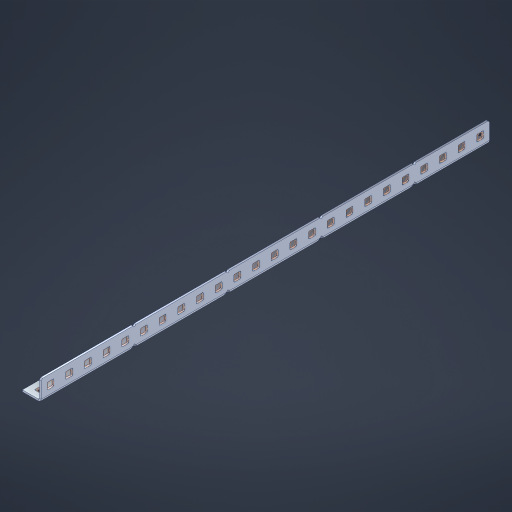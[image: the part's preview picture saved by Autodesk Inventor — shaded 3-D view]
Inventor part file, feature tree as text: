
AUTODESK INVENTOR PART (.ipt)
format: ipt  version: 2023 (Build 270158000, 158)  size: 823,808 bytes
history: native  units: in
note: dims shown in document units (in); Inventor stores cm internally (conversion verified against a paired STEP export)
features: other x53, extrude x47, sheet_metal_op x10, sketch x8, mirror x1, pattern_linear x1, chamfer x1
ambient origin geometry x8: Origin, YZ Plane, XZ Plane, XY Plane, X Axis, Y Axis, Z Axis, Center Point
bodies: Solid1 (feature_tree), Body (feature_tree)
feature tree (121):
  other  "Flange Pattern Plane"
  sheet_metal_op  "Flange Pattern"
  sheet_metal_op  "Body Pattern"
  other  "Arc Length"
  mirror  "Notch Mirror"
  pattern_linear  "Notch Pattern"  Spacing1=0.1875in  [1 undecoded]
  chamfer  "End Chamfer"
  extrude  "Half Cut"  Depth=0.0469in
  sketch  "Sketch1"  dims[d0=2.5in]
  other  "Plate1"
  sketch  "Sketch2"  dims[d1=12.0in]
  other  "Plate2"
  sheet_metal_op  "Bend1"
  sheet_metal_op  "Corner1"
  sketch  "Sketch3"  dims[d2=0.0469in]
  other  "Flange Pattern Sketch"
  sketch  "Sketch7"  dims[d3=0.0469in]
  other  "Srf1"
  other  "Srf2"
  sketch  "Sketch8"  dims[d4=0.0234in]
  sketch  "Sketch9"  dims[d5=0.0938in]
  other  "Srf91"
  sheet_metal_op  "Body Pattern Sketch"
  other  "Srf92"
  sketch  "Sketch13"  dims[d6=0.0469in]
  sketch  "Sketch14"  dims[d7=0.5in d8=90.0deg d9=0.0312in d10=0.1875in d11=0.0469in d12=0.0469in d16=0.182in d17=0.02in d18=0.0469in d19=0.0in d20=0.25in d21=0.25in d46=0.172in d47=1.0in d48=0.0in d49=0.182in d50=0.02in d51=0.25in d52=0.25in d53=0.0469in d54=0.0in d55=0.172in d56=1.0in d57=0.0in d60=9.4488in d62=0.5in d63=0.3937in d65=0.5in d85=0.1227in d86=0.1659in d88=0.04in d89=0.0469in d90=0.0in d91=0.04in d92=0.0491in d95=2.5in d96=0.04in d97=0.25in d98=45.0deg d101=0.0in d102=2.497in d131=0.5in d132=9.4488in d134=0.5in d139=0.5in]
  other  "Srf856"
  other  "Srf1310"
  other  "Srf1311"
  other  "Srf1312"
  other  "Srf1376"
  other  "Srf1377"
  other  "Srf1728"
  other  "Srf1755"
  other  "Srf1878"
  other  "Srf1879"
  other  "Srf1880"
  other  "Srf1881"
  other  "Srf1882"
  other  "Srf1883"
  other  "Srf1884"
  other  "Srf1885"
  other  "Srf1886"
  other  "Srf1887"
  other  "Srf1888"
  other  "Srf1889"
  other  "Srf1890"
  other  "Srf1891"
  other  "Srf1892"
  other  "Srf1893"
  other  "Srf1894"
  other  "Srf1895"
  other  "Srf1942"
  other  "Srf1943"
  other  "Srf1944"
  other  "Srf1945"
  other  "Srf1946"
  other  "Srf1947"
  other  "Srf1948"
  other  "Srf1949"
  other  "Srf1950"
  other  "Srf1951"
  other  "Srf1952"
  other  "Srf1953"
  other  "Srf1954"
  other  "Srf1955"
  other  "Srf1956"
  other  "Srf1957"
  other  "Srf1958"
  other  "Srf1959"
  sheet_metal_op  "Flange Stamp"
  sheet_metal_op  "Flange Circle"
  sheet_metal_op  "Body Stamp"
  sheet_metal_op  "Body Circle"
  sheet_metal_op  "Notch"
  extrude  "ExtrusionSrf2"  Depth=0.0469in
  extrude  "ExtrusionSrf92"  Depth=0.5in
  extrude  "ExtrusionSrf856"  Depth=0.02in
  extrude  "ExtrusionSrf1310"  Depth=0.0469in
  extrude  "ExtrusionSrf1311"  TaperAngle=0.0deg  [1 undecoded]
  extrude  "ExtrusionSrf1312"  Depth=0.5in
  extrude  "ExtrusionSrf1376"  Depth=0.5in
  extrude  "ExtrusionSrf1377"  Depth=0.5in
  extrude  "ExtrusionSrf1728"  Depth=0.5in TaperAngle=0.0deg
  extrude  "ExtrusionSrf1755"  Depth=0.5in
  extrude  "ExtrusionSrf1878"  Depth=0.02in
  extrude  "ExtrusionSrf1879"  Depth=0.5in
  extrude  "ExtrusionSrf1880"  Depth=0.5in
  extrude  "ExtrusionSrf1881"  Depth=0.0469in
  extrude  "ExtrusionSrf1882"  TaperAngle=0.0deg  [1 undecoded]
  extrude  "ExtrusionSrf1883"  Depth=0.5in
  extrude  "ExtrusionSrf1884"  Depth=0.5in TaperAngle=0.0deg
  extrude  "ExtrusionSrf1885"  Depth=0.5in
  extrude  "ExtrusionSrf1886"  Depth=0.5in
  extrude  "ExtrusionSrf1887"  Depth=0.5in
  extrude  "ExtrusionSrf1888"  Depth=0.5in
  extrude  "ExtrusionSrf1889"  Depth=0.5in
  extrude  "ExtrusionSrf1890"  Depth=0.0469in
  extrude  "ExtrusionSrf1891"  TaperAngle=0.0deg  [1 undecoded]
  extrude  "ExtrusionSrf1892"  Depth=0.5in
  extrude  "ExtrusionSrf1893"  Depth=0.5in
  extrude  "ExtrusionSrf1894"  Depth=0.5in
  extrude  "ExtrusionSrf1895"  Depth=0.5in TaperAngle=45.0deg
  extrude  "ExtrusionSrf1942"  TaperAngle=0.0deg  [1 undecoded]
  extrude  "ExtrusionSrf1943"  Depth=0.5in
  extrude  "ExtrusionSrf1944"  Depth=0.5in
  extrude  "ExtrusionSrf1945"  Depth=0.5in
  extrude  "ExtrusionSrf1946"  Depth=0.5in
  extrude  "ExtrusionSrf1947"  Depth=0.5in
  extrude  "ExtrusionSrf1948"  [1 undecoded]
  extrude  "ExtrusionSrf1949"  [1 undecoded]
  extrude  "ExtrusionSrf1950"  [1 undecoded]
  extrude  "ExtrusionSrf1951"  [1 undecoded]
  extrude  "ExtrusionSrf1952"  [1 undecoded]
  extrude  "ExtrusionSrf1953"  [1 undecoded]
  extrude  "ExtrusionSrf1954"  [1 undecoded]
  extrude  "ExtrusionSrf1955"  [1 undecoded]
  extrude  "ExtrusionSrf1956"  [1 undecoded]
  extrude  "ExtrusionSrf1957"  [1 undecoded]
  extrude  "ExtrusionSrf1958"  [1 undecoded]
  extrude  "ExtrusionSrf1959"  [1 undecoded]
note: 17 required parameter values undecoded (feature->parameter linkage not recoverable at this tier; creation-order binding heuristic only, values carry confidence <= 0.55)
